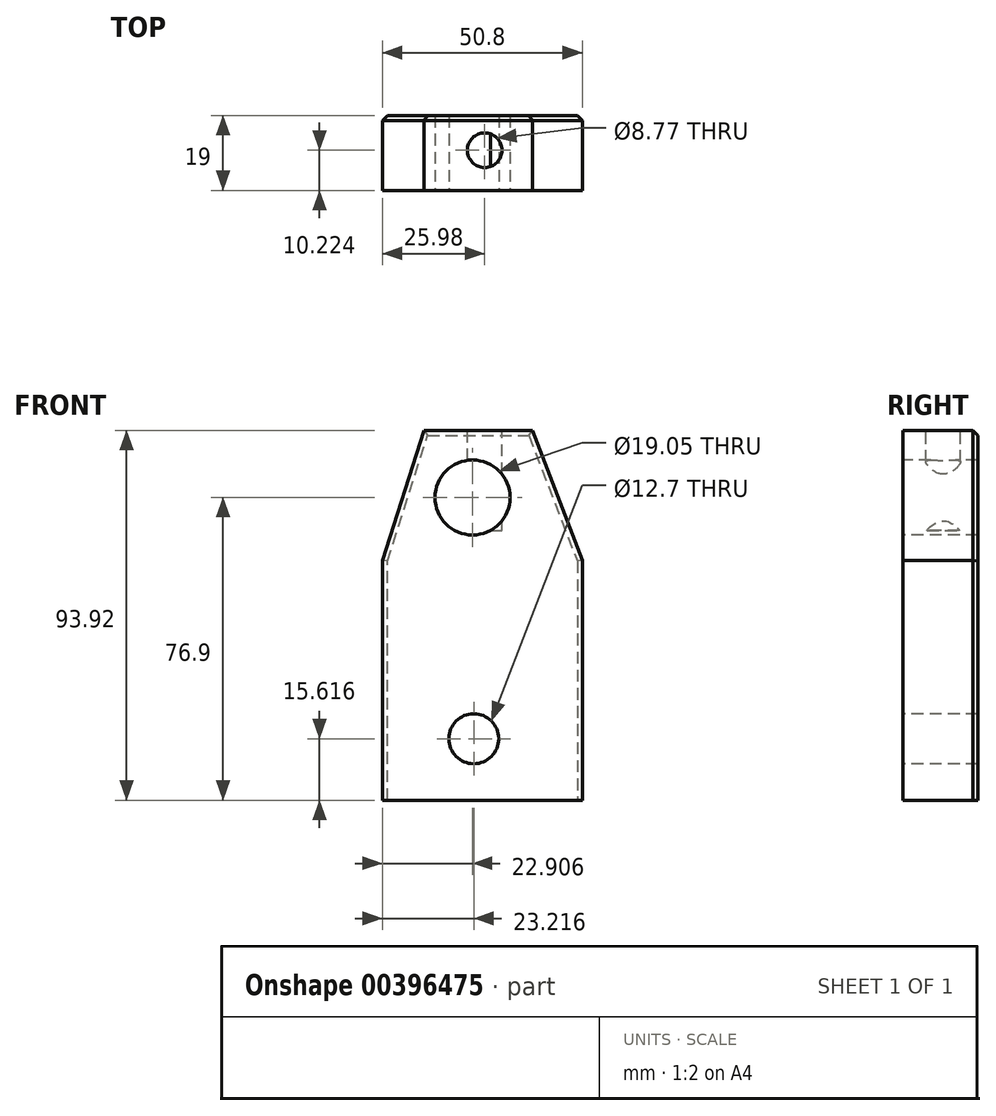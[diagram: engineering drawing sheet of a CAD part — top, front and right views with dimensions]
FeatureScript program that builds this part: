
annotation { "Feature Type Name" : "Feature", "Feature Type Description" : "" }
export const myFeature = defineFeature(function(context is Context, id is Id, definition is map)
    precondition{}
    {
        {
            var Q0;
            Q0=qCreatedBy(makeId("Front.planeOp"),FACE);
            var sketch = newSketch(context, id + "F0", { "sketchPlane" : qUnion([Q0])});
            skLineSegment(sketch, "E0", {"start": v(-52.62, -60.96) * mm, "end": v(-1.82, -60.96) * mm});
            skLineSegment(sketch, "E1", {"start": v(-1.82, -60.96) * mm, "end": v(-1.82, 0) * mm});
            skLineSegment(sketch, "E2", {"start": v(-52.62, -60.96) * mm, "end": v(-52.62, 0) * mm});
            skLineSegment(sketch, "E3", {"start": v(-34.67, 32.96) * mm, "end": v(-14.55, 32.96) * mm});
            skLineSegment(sketch, "E4", {"start": v(-14.55, 32.96) * mm, "end": v(-1.82, 0) * mm});
            skLineSegment(sketch, "E5", {"start": v(-42.1, 32.96) * mm, "end": v(-52.62, 0) * mm});
            skLineSegment(sketch, "E6", {"start": v(-42.1, 32.96) * mm, "end": v(-34.67, 32.96) * mm});
            skSolve(sketch);
        }
        {
            var Q0;
            Q0=makeQuery(id+"F0.imprint","IMPRINT",FACE,{"disambiguationData":[TD([[makeQuery(id+"F0.imprint","IMPRINT",EDGE,{"derivedFrom":sQuery(id+"F0.wireOp",EDGE,"E0")}),1.0]])]});
            extrude(context, id + "F1", {"entities" : qUnion([Q0]), "depth" : 19 * mm});
        }
        {
            var Q0;
            Q0=makeQuery(id+"F1.opExtrude","CAP_FACE",FACE,{"disambiguationData":[OSD([sQuery(id+"F0.wireOp",EDGE,"E0"),sQuery(id+"F0.wireOp",EDGE,"E1"),sQuery(id+"F0.wireOp",EDGE,"E2"),sQuery(id+"F0.wireOp",EDGE,"E3"),sQuery(id+"F0.wireOp",EDGE,"E4"),sQuery(id+"F0.wireOp",EDGE,"E5"),sQuery(id+"F0.wireOp",EDGE,"E6")])],"isStart":false});
            var sketch = newSketch(context, id + "F2", { "sketchPlane" : qUnion([Q0])});
            skCircle(sketch, "E7", {"center": v(-29.71, 15.94) * mm, "radius": 9.53 * mm});
            skCircle(sketch, "E8", {"center": v(-29.4, -45.34) * mm, "radius": 6.35 * mm});
            skSolve(sketch);
        }
        {
            var Q0;
            Q0=sQuery(id+"F2.wireOp",VERTEX,"E7.center");
            var Q1;
            Q1=makeQuery(id+"F1.opExtrude","SWEPT_BODY",BODY,{"disambiguationData":[OSD([sQuery(id+"F0.wireOp",EDGE,"E0"),sQuery(id+"F0.wireOp",EDGE,"E1"),sQuery(id+"F0.wireOp",EDGE,"E2"),sQuery(id+"F0.wireOp",EDGE,"E3"),sQuery(id+"F0.wireOp",EDGE,"E4"),sQuery(id+"F0.wireOp",EDGE,"E5"),sQuery(id+"F0.wireOp",EDGE,"E6")])]});
            hole(context, id + "F3", {"style" : HoleStyle.SIMPLE, "endStyle" : HoleEndStyle.THROUGH, "holeDiameter" : 19.05 * mm, "isTappedThrough" : true, "tappedDepth" : 12.7 * mm, "tapClearance" : 3, "locations" : qUnion([Q0]), "scope" : qUnion([Q1])});
        }
        {
            var Q0;
            Q0=sQuery(id+"F2.wireOp",VERTEX,"E8.center");
            var Q1;
            Q1=makeQuery(id+"F1.opExtrude","SWEPT_BODY",BODY,{"disambiguationData":[OSD([sQuery(id+"F0.wireOp",EDGE,"E0"),sQuery(id+"F0.wireOp",EDGE,"E1"),sQuery(id+"F0.wireOp",EDGE,"E2"),sQuery(id+"F0.wireOp",EDGE,"E3"),sQuery(id+"F0.wireOp",EDGE,"E4"),sQuery(id+"F0.wireOp",EDGE,"E5"),sQuery(id+"F0.wireOp",EDGE,"E6")])]});
            hole(context, id + "F4", {"style" : HoleStyle.SIMPLE, "endStyle" : HoleEndStyle.THROUGH, "holeDiameter" : 12.7 * mm, "isTappedThrough" : true, "tappedDepth" : 12.7 * mm, "tapClearance" : 3, "locations" : qUnion([Q0]), "scope" : qUnion([Q1])});
        }
        {
            var Q0;
            Q0=makeQuery(id+"F1.opExtrude","SWEPT_FACE",FACE,{"disambiguationData":[OSD([sQuery(id+"F0.wireOp",EDGE,"E3"),sQuery(id+"F0.wireOp",EDGE,"E6")])]});
            var sketch = newSketch(context, id + "F5", { "sketchPlane" : qUnion([Q0])});
            skCircle(sketch, "E9", {"center": v(-26.64, -8.78) * mm, "radius": 4.39 * mm});
            skSolve(sketch);
        }
        {
            var Q0;
            Q0 = qSketchRegion(id + "F5", true);
            extrude(context, id + "F6", {"entities" : qUnion([Q0]), "operationType" : NewBodyOperationType.REMOVE, "oppositeDirection" : true, "depth" : 25.4 * mm});
        }
        {
            var Q0;
            Q0=makeQuery(id+"F1.opExtrude","CAP_EDGE",EDGE,{"disambiguationData":[OSD([sQuery(id+"F0.wireOp",EDGE,"E5")])],"isStart":true});
            var Q1;
            Q1=makeQuery(id+"F1.opExtrude","CAP_EDGE",EDGE,{"disambiguationData":[OSD([sQuery(id+"F0.wireOp",EDGE,"E2")])],"isStart":true});
            var Q2;
            Q2=makeQuery(id+"F1.opExtrude","CAP_EDGE",EDGE,{"disambiguationData":[OSD([sQuery(id+"F0.wireOp",EDGE,"E1")])],"isStart":true});
            var Q3;
            Q3=makeQuery(id+"F1.opExtrude","CAP_EDGE",EDGE,{"disambiguationData":[OSD([sQuery(id+"F0.wireOp",EDGE,"E4")])],"isStart":true});
            var Q4;
            Q4=makeQuery(id+"F1.opExtrude","CAP_EDGE",EDGE,{"disambiguationData":[OSD([sQuery(id+"F0.wireOp",EDGE,"E3"),sQuery(id+"F0.wireOp",EDGE,"E6")])],"isStart":true});
            var Q5;
            Q5=makeQuery(id+"F3.hole-0.boolean.opBoolean","INTERSECT",EDGE,{"derivedFrom":[makeQuery(id+"F1.opExtrude","CAP_FACE",FACE,{"disambiguationData":[OSD([sQuery(id+"F0.wireOp",EDGE,"E0"),sQuery(id+"F0.wireOp",EDGE,"E1"),sQuery(id+"F0.wireOp",EDGE,"E2"),sQuery(id+"F0.wireOp",EDGE,"E3"),sQuery(id+"F0.wireOp",EDGE,"E4"),sQuery(id+"F0.wireOp",EDGE,"E5"),sQuery(id+"F0.wireOp",EDGE,"E6")])],"isStart":true}),makeQuery(id+"F3.hole-0.opRevolve","SWEPT_FACE",FACE,{"disambiguationData":[OSD([sQuery(id+"F3.hole-0.sketch.wireOp",EDGE,"core_line_2")])]})]});
            var Q6;
            Q6=makeQuery(id+"F4.hole-0.boolean.opBoolean","INTERSECT",EDGE,{"derivedFrom":[makeQuery(id+"F1.opExtrude","CAP_FACE",FACE,{"disambiguationData":[OSD([sQuery(id+"F0.wireOp",EDGE,"E0"),sQuery(id+"F0.wireOp",EDGE,"E1"),sQuery(id+"F0.wireOp",EDGE,"E2"),sQuery(id+"F0.wireOp",EDGE,"E3"),sQuery(id+"F0.wireOp",EDGE,"E4"),sQuery(id+"F0.wireOp",EDGE,"E5"),sQuery(id+"F0.wireOp",EDGE,"E6")])],"isStart":true}),makeQuery(id+"F4.hole-0.opRevolve","SWEPT_FACE",FACE,{"disambiguationData":[OSD([sQuery(id+"F4.hole-0.sketch.wireOp",EDGE,"core_line_2")])]})]});
            var Q7;
            Q7=makeQuery(id+"F3.hole-0.boolean.opBoolean","COPY",EDGE,{"derivedFrom":makeQuery(id+"F3.hole-0.opRevolve","SWEPT_EDGE",EDGE,{"disambiguationData":[OSD([sQuery(id+"F3.hole-0.sketch.wireOp",EDGE,"core_line_2"),sQuery(id+"F3.hole-0.sketch.wireOp",EDGE,"core_line_3")])]})});
            var Q8;
            Q8=makeQuery(id+"F4.hole-0.boolean.opBoolean","COPY",EDGE,{"derivedFrom":makeQuery(id+"F4.hole-0.opRevolve","SWEPT_EDGE",EDGE,{"disambiguationData":[OSD([sQuery(id+"F4.hole-0.sketch.wireOp",EDGE,"core_line_2"),sQuery(id+"F4.hole-0.sketch.wireOp",EDGE,"core_line_3")])]})});
            chamfer(context, id + "F7", {"entities" : qUnion([Q0, Q1, Q2, Q3, Q4, Q5, Q6, Q7, Q8]), "width" : 1.27 * mm, "tangentPropagation" : true});
        }
    });
